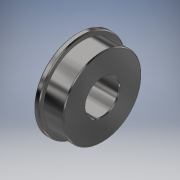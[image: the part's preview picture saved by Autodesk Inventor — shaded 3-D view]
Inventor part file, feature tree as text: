
AUTODESK INVENTOR PART (.ipt)
format: ipt  version: 2018 (Build 220112000, 112)  size: 157,184 bytes
history: native  units: in
note: dims shown in document units (in); Inventor stores cm internally (conversion verified against a paired STEP export)
features: chamfer x1, other x1, imported_body x1
ambient origin geometry x8: Origin, YZ Plane, XZ Plane, XY Plane, X Axis, Y Axis, Z Axis, Center Point
bodies: Body1 (feature_tree)
feature tree (3):
  chamfer  "Chamfer1"  [1 undecoded]
  other  "FR6ZZ Bearing_smart.ipt1"
  imported_body  "Base1"
note: 1 required parameter value undecoded (feature->parameter linkage not recoverable at this tier; creation-order binding heuristic only, values carry confidence <= 0.55)
